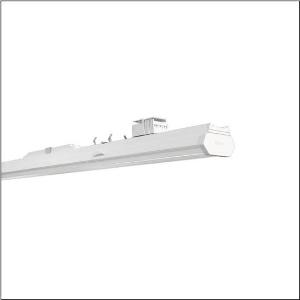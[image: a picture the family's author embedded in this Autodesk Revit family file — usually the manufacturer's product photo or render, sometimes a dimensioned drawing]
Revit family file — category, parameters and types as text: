
# Revit family: licross_r__21_protected_ho_52td12cn4cxm_6843
name_source: partatom
category: Lighting Fixtures
units: mm (PartAtom-declared; Revit-internal decimal feet)

## family parameters
Cut with Voids When Loaded = No
Host = Face
Light Source = No
Part Type = Normal
Room Calculation Point = No
Round Connector Dimension = Use Diameter
Shared = No

## types (1)
- --- (1 x LED, 12460 lm, 68.9 W, 4000K)
    Apparent Load = 69 VA
    CIE Flux Codes = 70 91 97 98 100
    Color Rendering = 80
    Color Temperature = 4000K
    Default Elevation = 1800 mm
    Description = Licross® 21 Protected HO, luminaire insert, of sheet steel, galvanised, coil coated, white, length: 1.500mm, width: 90mm, height: 103mm, LED rated luminous flux: 12.460lm, light colour: 840, control gear: ON/OFF Multilumen, CLOi, control gear: ECG Multilumen, with plug, 3-pole, with phase selection, mains connection: 220..240V, AC, 50/60Hz, start of lifetime: 69W, end of service life: 83W, halogen-free wiring, primary light control with lens, of plastic, primary optical cover: cover, of PMMA, light emission: direct distribution, primary light characteristic: symmetric, protection rating (complete): IP54, insulation class (complete): insulation class I (protective earthing), certification: CE, ENEC, VDE, UKCA, protection symbol: D if used in an environment with non-conductive dust loads with corresponding accessories, impact resistance: IK06, permissible ambient temperature for indoor applications: -35..+35°C, corresponds to IFS (International Featured Standards) requirements for safety and quality in the food industry, reducing of maximum allowable ambient temperature of 5°C with ceiling mounting, LABS conformity tested according to VDMA 24364:2018-05, packaging unit: 1 piece
    Height = 92 mm
    Lamp = 1 x LED
    Lamp Light Flux = 12460 lm
    Lamp Power = 68.9 W
    Lamp count = 1
    Length = 1500 mm
    Luminous efficacy = 181 lm/W
    Manufacturer = Siteco
    ModVariant = No
    Model = 52TD12CN4CXM
    Mounting Place = Ceiling
    Mounting Type = Pendant
    Number of Poles = 1
    OnlyDefault = Yes
    Power Factor = 1
    Product Name = Licross® 21 Protected HO
    Product group = luminaire insert
    ProductGroupID = 901
    Protection Class = Protection class I
    Protection Degree = IP 54
    RLX_Detail_Level = 1
    RLX_Emergency_Light_Flux = 0 lm
    RLX_Emergency_Type = 0
    RLX_Emergency_Type_DB = No
    RlxData = <blob elided: 22121 chars, md5=6820b56d>
    Socket = socket
    Standby Power = 0 W
    System Light Flux = 12460 lm
    System Power = 69 W
    Type Comments = factory setting: luminous flux: 100 % | (A | C | E) | 162 mA
    Type Image = l_1256148.jpg
    URL = http://relux.com
    VarID = @adj_059743
    Voltage = 0 V
    Weight = 0.00 kg
    Width = 88 mm

## geometry (parser evidence)
native form markers: Blend x4, Sweep x10
no freeform markers — native parametric forms only
